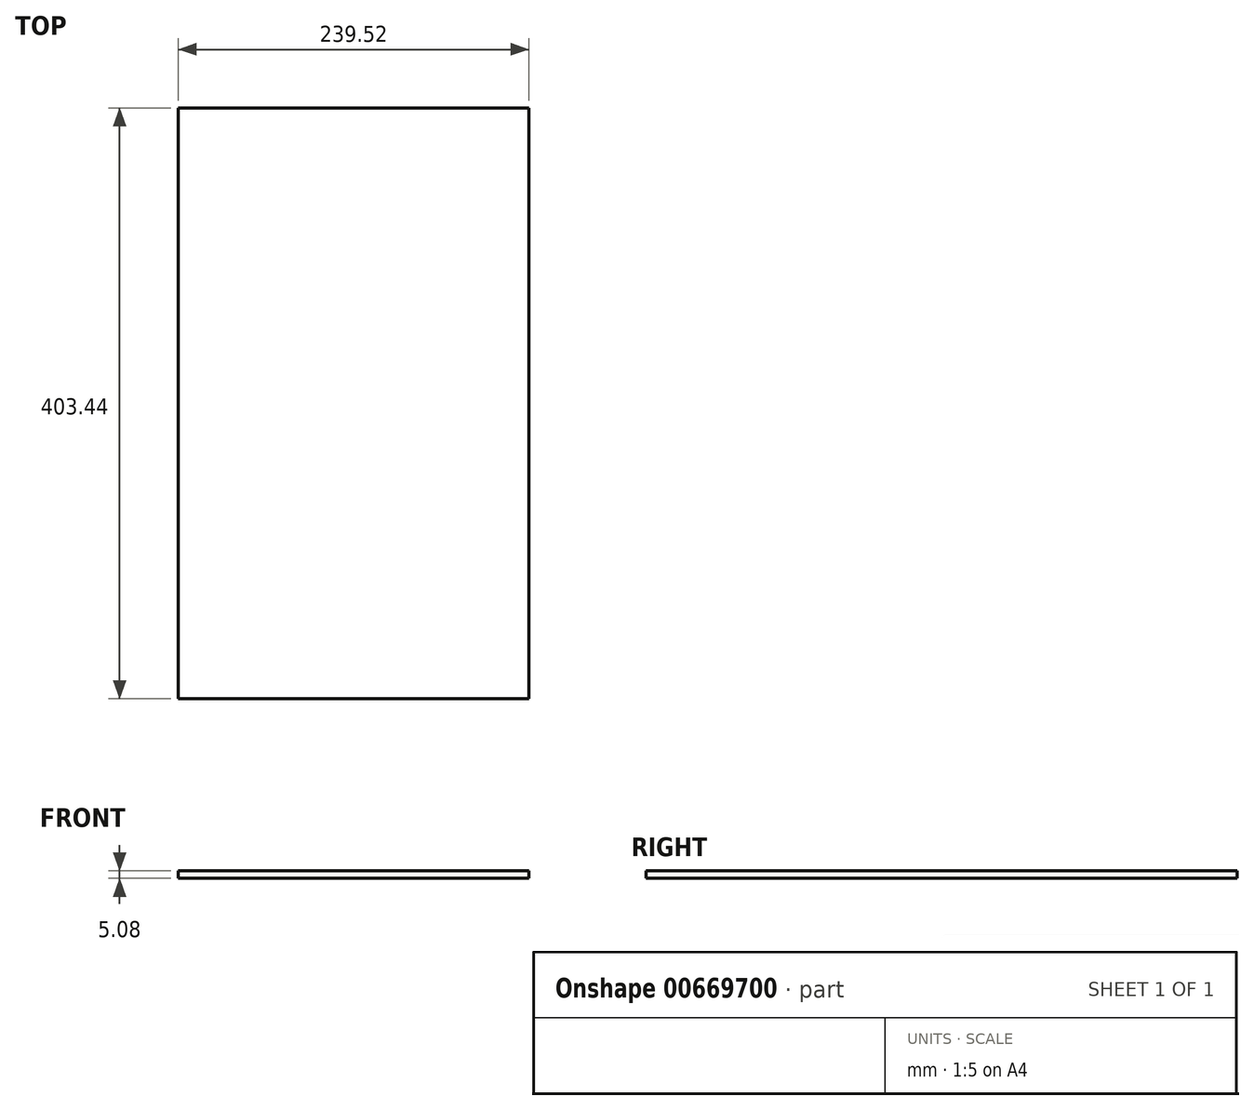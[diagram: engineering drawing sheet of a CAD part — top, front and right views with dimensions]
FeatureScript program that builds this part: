
annotation { "Feature Type Name" : "Feature", "Feature Type Description" : "" }
export const myFeature = defineFeature(function(context is Context, id is Id, definition is map)
    precondition{}
    {
        {
            var Q0;
            Q0=qCreatedBy(makeId("Top.planeOp"),FACE);
            var sketch = newSketch(context, id + "F0", { "sketchPlane" : qUnion([Q0])});
            skLineSegment(sketch, "E0.bottom", {"start": v(-119.76, 201.72) * mm, "end": v(119.76, 201.72) * mm});
            skLineSegment(sketch, "E0.top", {"start": v(-119.76, -201.72) * mm, "end": v(119.76, -201.72) * mm});
            skLineSegment(sketch, "E0.left", {"start": v(-119.76, 201.72) * mm, "end": v(-119.76, -201.72) * mm});
            skLineSegment(sketch, "E0.right", {"start": v(119.76, 201.72) * mm, "end": v(119.76, -201.72) * mm});
            skPoint(sketch, "E0.middle", {"position": v(0, 0) * mm});
            skSolve(sketch);
        }
        {
            var Q0;
            Q0=makeQuery(id+"F0.imprint","IMPRINT",FACE,{"disambiguationData":[TD([[makeQuery(id+"F0.imprint","IMPRINT",EDGE,{"derivedFrom":sQuery(id+"F0.wireOp",EDGE,"E0.bottom")}),-1.0]])]});
            var Q1;
            Q1 = qSketchRegion(id + "F0", true);
            extrude(context, id + "F1", {"entities" : qUnion([Q0, Q1]), "depth" : 5.08 * mm, "offsetDistance" : 25.4 * mm});
        }
    });
